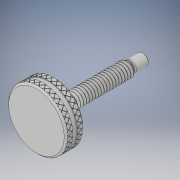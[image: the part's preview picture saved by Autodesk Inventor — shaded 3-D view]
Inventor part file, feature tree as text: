
AUTODESK INVENTOR PART (.ipt)
format: ipt  version: 2019 (Build 230136000, 136)  size: 2,494,976 bytes
history: native  units: in
note: dims shown in document units (in); Inventor stores cm internally (conversion verified against a paired STEP export)
features: chamfer x1, other x1
ambient origin geometry x8: Origin, YZ Plane, XZ Plane, XY Plane, X Axis, Y Axis, Z Axis, Center Point
bodies: Solid1 (feature_tree), Solid2 (feature_tree)
feature tree (2):
  chamfer  "Chamfer4"  [1 undecoded]
  other  "Cut-Revolve2"
note: 1 required parameter value undecoded (feature->parameter linkage not recoverable at this tier; creation-order binding heuristic only, values carry confidence <= 0.55)
